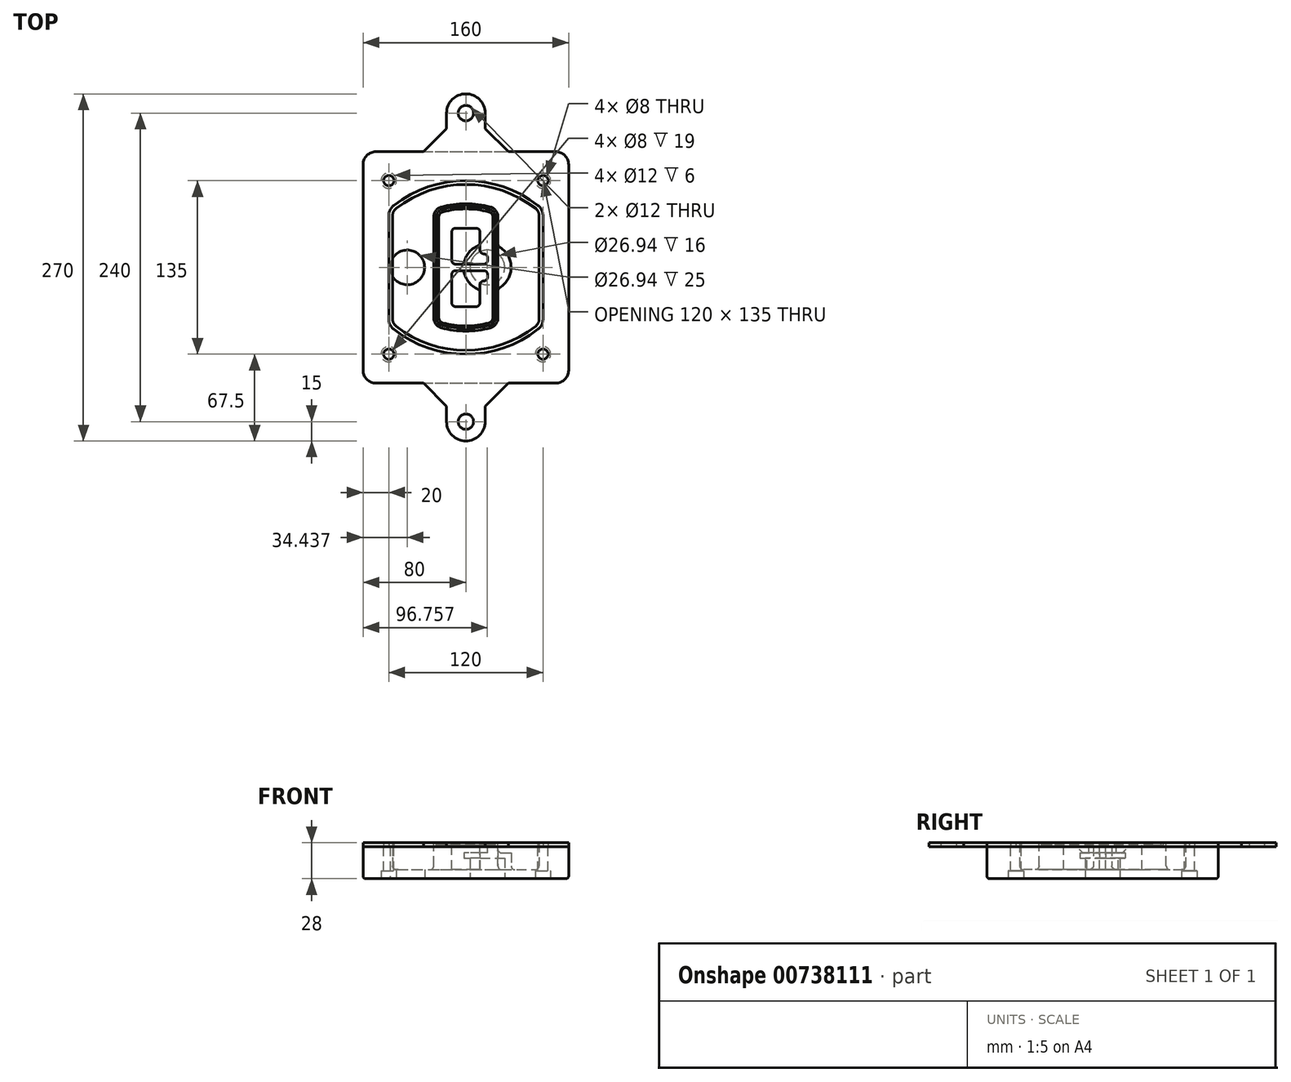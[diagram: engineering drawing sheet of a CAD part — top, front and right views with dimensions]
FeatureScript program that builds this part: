
annotation { "Feature Type Name" : "Feature", "Feature Type Description" : "" }
export const myFeature = defineFeature(function(context is Context, id is Id, definition is map)
    precondition{}
    {
        {
            var Q0;
            Q0=qCreatedBy(makeId("Top.planeOp"),FACE);
            var sketch = newSketch(context, id + "F0", { "sketchPlane" : qUnion([Q0])});
            skPoint(sketch, "E0.rect.middle", {"position": v(0, 0) * mm});
            skLineSegment(sketch, "E1.bottom", {"start": v(-70, -90) * mm, "end": v(70, -90) * mm});
            skLineSegment(sketch, "E1.top", {"start": v(-70, 90) * mm, "end": v(70, 90) * mm});
            skLineSegment(sketch, "E1.left", {"start": v(-80, -80) * mm, "end": v(-80, 80) * mm});
            skLineSegment(sketch, "E1.right", {"start": v(80, -80) * mm, "end": v(80, 80) * mm});
            skLineSegment(sketch, "E2", {"start": v(-80, 90) * mm, "end": v(80, -90) * mm, "construction": true});
            skLineSegment(sketch, "E3", {"start": v(80, 90) * mm, "end": v(-80, -90) * mm, "construction": true});
            skCircle(sketch, "E4", {"center": v(-60, 67.5) * mm, "radius": 4 * mm});
            skCircle(sketch, "E5", {"center": v(60, 67.5) * mm, "radius": 4 * mm});
            skCircle(sketch, "E6", {"center": v(60, -67.5) * mm, "radius": 4 * mm});
            skCircle(sketch, "E7", {"center": v(-60, -67.5) * mm, "radius": 4 * mm});
            skLineSegment(sketch, "E8", {"start": v(-60, 67.5) * mm, "end": v(60, 67.5) * mm, "construction": true});
            skLineSegment(sketch, "E9", {"start": v(60, 67.5) * mm, "end": v(60, -67.5) * mm, "construction": true});
            skLineSegment(sketch, "E10", {"start": v(60, -67.5) * mm, "end": v(-60, -67.5) * mm, "construction": true});
            skLineSegment(sketch, "E11", {"start": v(-60, -67.5) * mm, "end": v(-60, 67.5) * mm, "construction": true});
            skLineSegment(sketch, "E12", {"start": v(-60, 40.3) * mm, "end": v(-60, -40.3) * mm});
            skLineSegment(sketch, "E13", {"start": v(60, 40.3) * mm, "end": v(60, -40.3) * mm});
            skArc(sketch, "E14", {"start": v(56.15, 48.18) * mm, "mid": v(0, 67.5) * mm, "end": v(-56.15, 48.18) * mm});
            skArc(sketch, "E15", {"start": v(-56.15, -48.18) * mm, "mid": v(0, -67.5) * mm, "end": v(56.15, -48.18) * mm});
            skLineSegment(sketch, "E16", {"start": v(-60, 0) * mm, "end": v(60, 0) * mm, "construction": true});
            skPoint(sketch, "E17.visualSharp", {"position": v(-60, -45) * mm});
            skArc(sketch, "E17.filletArc", {"start": v(-60, -40.3) * mm, "mid": v(-58.99, -44.68) * mm, "end": v(-56.15, -48.18) * mm});
            skPoint(sketch, "E18.visualSharp", {"position": v(-60, 45) * mm});
            skArc(sketch, "E18.filletArc", {"start": v(-56.15, 48.18) * mm, "mid": v(-58.99, 44.68) * mm, "end": v(-60, 40.3) * mm});
            skPoint(sketch, "E19.visualSharp", {"position": v(60, 45) * mm});
            skArc(sketch, "E19.filletArc", {"start": v(60, 40.3) * mm, "mid": v(58.99, 44.68) * mm, "end": v(56.15, 48.18) * mm});
            skPoint(sketch, "E20.visualSharp", {"position": v(60, -45) * mm});
            skArc(sketch, "E20.filletArc", {"start": v(56.15, -48.18) * mm, "mid": v(58.99, -44.68) * mm, "end": v(60, -40.3) * mm});
            skPoint(sketch, "E21.visualSharp", {"position": v(-80, 90) * mm});
            skArc(sketch, "E21.filletArc", {"start": v(-70, 90) * mm, "mid": v(-77.07, 87.07) * mm, "end": v(-80, 80) * mm});
            skPoint(sketch, "E22.visualSharp", {"position": v(80, 90) * mm});
            skArc(sketch, "E22.filletArc", {"start": v(80, 80) * mm, "mid": v(77.07, 87.07) * mm, "end": v(70, 90) * mm});
            skPoint(sketch, "E23.visualSharp", {"position": v(80, -90) * mm});
            skArc(sketch, "E23.filletArc", {"start": v(70, -90) * mm, "mid": v(77.07, -87.07) * mm, "end": v(80, -80) * mm});
            skPoint(sketch, "E24.visualSharp", {"position": v(-80, -90) * mm});
            skArc(sketch, "E24.filletArc", {"start": v(-80, -80) * mm, "mid": v(-77.07, -87.07) * mm, "end": v(-70, -90) * mm});
            skArc(sketch, "E25.0", {"start": v(57, 40.3) * mm, "mid": v(56.3, 43.36) * mm, "end": v(54.3, 45.81) * mm});
            skLineSegment(sketch, "E25.1", {"start": v(57, 40.3) * mm, "end": v(57, -40.3) * mm});
            skArc(sketch, "E25.2", {"start": v(54.3, -45.81) * mm, "mid": v(56.3, -43.36) * mm, "end": v(57, -40.3) * mm});
            skArc(sketch, "E25.3", {"start": v(-54.3, -45.81) * mm, "mid": v(0, -64.5) * mm, "end": v(54.3, -45.81) * mm});
            skArc(sketch, "E25.4", {"start": v(-57, -40.3) * mm, "mid": v(-56.3, -43.36) * mm, "end": v(-54.3, -45.81) * mm});
            skArc(sketch, "E25.5", {"start": v(54.3, 45.81) * mm, "mid": v(0, 64.5) * mm, "end": v(-54.3, 45.81) * mm});
            skLineSegment(sketch, "E25.6", {"start": v(-57, 40.3) * mm, "end": v(-57, -40.3) * mm});
            skArc(sketch, "E25.7", {"start": v(-54.3, 45.81) * mm, "mid": v(-56.3, 43.36) * mm, "end": v(-57, 40.3) * mm});
            skArc(sketch, "E26.0", {"start": v(-58.62, 51.33) * mm, "mid": v(-62.58, 46.43) * mm, "end": v(-64, 40.3) * mm});
            skArc(sketch, "E26.1", {"start": v(58.62, 51.33) * mm, "mid": v(0, 71.5) * mm, "end": v(-58.62, 51.33) * mm});
            skArc(sketch, "E26.2", {"start": v(64, 40.3) * mm, "mid": v(62.58, 46.43) * mm, "end": v(58.62, 51.33) * mm});
            skLineSegment(sketch, "E26.3", {"start": v(64, 40.3) * mm, "end": v(64, -40.3) * mm});
            skArc(sketch, "E26.4", {"start": v(58.62, -51.33) * mm, "mid": v(62.58, -46.43) * mm, "end": v(64, -40.3) * mm});
            skLineSegment(sketch, "E26.5", {"start": v(-64, 40.3) * mm, "end": v(-64, -40.3) * mm});
            skArc(sketch, "E26.6", {"start": v(-58.62, -51.33) * mm, "mid": v(0, -71.5) * mm, "end": v(58.62, -51.33) * mm});
            skArc(sketch, "E26.7", {"start": v(-64, -40.3) * mm, "mid": v(-62.58, -46.43) * mm, "end": v(-58.62, -51.33) * mm});
            skSolve(sketch);
        }
        {
            var Q0;
            Q0=makeQuery(id+"F0.imprint","IMPRINT",FACE,{"disambiguationData":[TD([[makeQuery(id+"F0.imprint","IMPRINT",EDGE,{"derivedFrom":sQuery(id+"F0.wireOp",EDGE,"E1.bottom")}),1.0]])]});
            var Q1;
            Q1=makeQuery(id+"F0.imprint","IMPRINT",FACE,{"disambiguationData":[TD([[makeQuery(id+"F0.imprint","IMPRINT",EDGE,{"derivedFrom":sQuery(id+"F0.wireOp",EDGE,"E12")}),1.0]])]});
            var Q2;
            Q2=makeQuery(id+"F0.imprint","IMPRINT",FACE,{"disambiguationData":[TD([[makeQuery(id+"F0.imprint","IMPRINT",EDGE,{"derivedFrom":sQuery(id+"F0.wireOp",EDGE,"E25.0")}),1.0]])]});
            var Q3;
            Q3=makeQuery(id+"F0.imprint","IMPRINT",FACE,{"disambiguationData":[TD([[makeQuery(id+"F0.imprint","IMPRINT",EDGE,{"derivedFrom":sQuery(id+"F0.wireOp",EDGE,"E12")}),-1.0]])]});
            extrude(context, id + "F1", {"entities" : qUnion([Q0, Q1, Q2, Q3]), "oppositeDirection" : true, "depth" : 25 * mm});
        }
        {
            var Q0;
            Q0=makeQuery(id+"F0.imprint","IMPRINT",FACE,{"disambiguationData":[TD([[makeQuery(id+"F0.imprint","IMPRINT",EDGE,{"derivedFrom":sQuery(id+"F0.wireOp",EDGE,"E12")}),1.0]])]});
            extrude(context, id + "F2", {"entities" : qUnion([Q0]), "operationType" : NewBodyOperationType.ADD, "depth" : 3 * mm});
        }
        {
            var Q0;
            Q0=makeQuery(id+"F0.imprint","IMPRINT",FACE,{"disambiguationData":[TD([[makeQuery(id+"F0.imprint","IMPRINT",EDGE,{"derivedFrom":sQuery(id+"F0.wireOp",EDGE,"E25.0")}),1.0]])]});
            extrude(context, id + "F3", {"entities" : qUnion([Q0]), "operationType" : NewBodyOperationType.REMOVE, "oppositeDirection" : true, "depth" : 18 * mm});
        }
        {
            var Q0;
            Q0=makeQuery(id+"F2.opExtrude","CAP_FACE",FACE,{"disambiguationData":[OSD([sQuery(id+"F0.wireOp",EDGE,"E12"),sQuery(id+"F0.wireOp",EDGE,"E13"),sQuery(id+"F0.wireOp",EDGE,"E14"),sQuery(id+"F0.wireOp",EDGE,"E15"),sQuery(id+"F0.wireOp",EDGE,"E17.filletArc"),sQuery(id+"F0.wireOp",EDGE,"E18.filletArc"),sQuery(id+"F0.wireOp",EDGE,"E19.filletArc"),sQuery(id+"F0.wireOp",EDGE,"E20.filletArc"),sQuery(id+"F0.wireOp",EDGE,"E25.0"),sQuery(id+"F0.wireOp",EDGE,"E25.1"),sQuery(id+"F0.wireOp",EDGE,"E25.2"),sQuery(id+"F0.wireOp",EDGE,"E25.3"),sQuery(id+"F0.wireOp",EDGE,"E25.4"),sQuery(id+"F0.wireOp",EDGE,"E25.5"),sQuery(id+"F0.wireOp",EDGE,"E25.6"),sQuery(id+"F0.wireOp",EDGE,"E25.7")])],"isStart":false});
            var sketch = newSketch(context, id + "F4", { "sketchPlane" : qUnion([Q0])});
            skArc(sketch, "E27.0", {"start": v(-19.08, -46.97) * mm, "mid": v(0, -49.5) * mm, "end": v(19.08, -46.97) * mm});
            skArc(sketch, "E28.0", {"start": v(19.08, 46.97) * mm, "mid": v(0, 49.5) * mm, "end": v(-19.08, 46.97) * mm});
            skLineSegment(sketch, "E29", {"start": v(-25, 39.25) * mm, "end": v(-25, -39.25) * mm});
            skLineSegment(sketch, "E30", {"start": v(25, 39.25) * mm, "end": v(25, -39.25) * mm});
            skLineSegment(sketch, "E31", {"start": v(-25, 45.1) * mm, "end": v(25, 45.1) * mm, "construction": true});
            skLineSegment(sketch, "E32", {"start": v(-25, -45.1) * mm, "end": v(25, -45.1) * mm, "construction": true});
            skPoint(sketch, "E33.visualSharp", {"position": v(-25, 45.1) * mm});
            skArc(sketch, "E33.filletArc", {"start": v(-19.08, 46.97) * mm, "mid": v(-23.35, 44.11) * mm, "end": v(-25, 39.25) * mm});
            skPoint(sketch, "E34.visualSharp", {"position": v(25, 45.1) * mm});
            skArc(sketch, "E34.filletArc", {"start": v(25, 39.25) * mm, "mid": v(23.35, 44.11) * mm, "end": v(19.08, 46.97) * mm});
            skPoint(sketch, "E35.visualSharp", {"position": v(25, -45.1) * mm});
            skArc(sketch, "E35.filletArc", {"start": v(19.08, -46.97) * mm, "mid": v(23.35, -44.11) * mm, "end": v(25, -39.25) * mm});
            skPoint(sketch, "E36.visualSharp", {"position": v(-25, -45.1) * mm});
            skArc(sketch, "E36.filletArc", {"start": v(-25, -39.25) * mm, "mid": v(-23.35, -44.11) * mm, "end": v(-19.08, -46.97) * mm});
            skArc(sketch, "E37.0", {"start": v(54.3, 45.81) * mm, "mid": v(0, 64.5) * mm, "end": v(-54.3, 45.81) * mm});
            skArc(sketch, "E37.1", {"start": v(-54.3, 45.81) * mm, "mid": v(-56.3, 43.36) * mm, "end": v(-57, 40.3) * mm});
            skLineSegment(sketch, "E37.2", {"start": v(-57, 40.3) * mm, "end": v(-57, -40.3) * mm});
            skArc(sketch, "E37.3", {"start": v(-57, -40.3) * mm, "mid": v(-56.3, -43.36) * mm, "end": v(-54.3, -45.81) * mm});
            skArc(sketch, "E37.4", {"start": v(-54.3, -45.81) * mm, "mid": v(0, -64.5) * mm, "end": v(54.3, -45.81) * mm});
            skArc(sketch, "E37.5", {"start": v(54.3, -45.81) * mm, "mid": v(56.3, -43.36) * mm, "end": v(57, -40.3) * mm});
            skLineSegment(sketch, "E37.6", {"start": v(57, 40.3) * mm, "end": v(57, -40.3) * mm});
            skArc(sketch, "E37.7", {"start": v(57, 40.3) * mm, "mid": v(56.3, 43.36) * mm, "end": v(54.3, 45.81) * mm});
            skLineSegment(sketch, "E38.0", {"start": v(23, 39.25) * mm, "end": v(23, -39.25) * mm});
            skArc(sketch, "E38.1", {"start": v(18.56, -45.04) * mm, "mid": v(21.76, -42.9) * mm, "end": v(23, -39.25) * mm});
            skArc(sketch, "E38.2", {"start": v(-18.56, -45.04) * mm, "mid": v(0, -47.5) * mm, "end": v(18.56, -45.04) * mm});
            skArc(sketch, "E38.3", {"start": v(-23, -39.25) * mm, "mid": v(-21.76, -42.9) * mm, "end": v(-18.56, -45.04) * mm});
            skLineSegment(sketch, "E38.4", {"start": v(-23, 39.25) * mm, "end": v(-23, -39.25) * mm});
            skArc(sketch, "E38.5", {"start": v(23, 39.25) * mm, "mid": v(21.76, 42.9) * mm, "end": v(18.56, 45.04) * mm});
            skArc(sketch, "E38.6", {"start": v(-18.56, 45.04) * mm, "mid": v(-21.76, 42.9) * mm, "end": v(-23, 39.25) * mm});
            skArc(sketch, "E38.7", {"start": v(18.56, 45.04) * mm, "mid": v(0, 47.5) * mm, "end": v(-18.56, 45.04) * mm});
            skArc(sketch, "E39.0", {"start": v(21, 39.25) * mm, "mid": v(20.18, 41.68) * mm, "end": v(18.04, 43.1) * mm});
            skLineSegment(sketch, "E39.1", {"start": v(21, 39.25) * mm, "end": v(21, -39.25) * mm});
            skArc(sketch, "E39.2", {"start": v(18.04, -43.1) * mm, "mid": v(20.18, -41.68) * mm, "end": v(21, -39.25) * mm});
            skArc(sketch, "E39.3", {"start": v(-18.04, -43.1) * mm, "mid": v(0, -45.5) * mm, "end": v(18.04, -43.1) * mm});
            skArc(sketch, "E39.4", {"start": v(-21, -39.25) * mm, "mid": v(-20.18, -41.68) * mm, "end": v(-18.04, -43.1) * mm});
            skArc(sketch, "E39.5", {"start": v(18.04, 43.1) * mm, "mid": v(0, 45.5) * mm, "end": v(-18.04, 43.1) * mm});
            skLineSegment(sketch, "E39.6", {"start": v(-21, 39.25) * mm, "end": v(-21, -39.25) * mm});
            skArc(sketch, "E39.7", {"start": v(-18.04, 43.1) * mm, "mid": v(-20.18, 41.68) * mm, "end": v(-21, 39.25) * mm});
            skLineSegment(sketch, "E40", {"start": v(-25, 0) * mm, "end": v(25, 0) * mm, "construction": true});
            skLineSegment(sketch, "E41", {"start": v(-11, 5.5) * mm, "end": v(-11, 27.5) * mm});
            skLineSegment(sketch, "E42", {"start": v(-8, 30.5) * mm, "end": v(8, 30.5) * mm});
            skLineSegment(sketch, "E43", {"start": v(11, 27.5) * mm, "end": v(11, 13.5) * mm});
            skLineSegment(sketch, "E44", {"start": v(14, 10.5) * mm, "end": v(14, 10.5) * mm});
            skLineSegment(sketch, "E45", {"start": v(17, 7.5) * mm, "end": v(17, 5.5) * mm});
            skLineSegment(sketch, "E46", {"start": v(14, 2.5) * mm, "end": v(-8, 2.5) * mm});
            skPoint(sketch, "E47.visualSharp", {"position": v(-11, 30.5) * mm});
            skArc(sketch, "E47.filletArc", {"start": v(-8, 30.5) * mm, "mid": v(-10.12, 29.62) * mm, "end": v(-11, 27.5) * mm});
            skPoint(sketch, "E48.visualSharp", {"position": v(11, 30.5) * mm});
            skArc(sketch, "E48.filletArc", {"start": v(11, 27.5) * mm, "mid": v(10.12, 29.62) * mm, "end": v(8, 30.5) * mm});
            skPoint(sketch, "E49.visualSharp", {"position": v(11, 10.5) * mm});
            skArc(sketch, "E49.filletArc", {"start": v(11, 13.5) * mm, "mid": v(11.88, 11.38) * mm, "end": v(14, 10.5) * mm});
            skPoint(sketch, "E50.visualSharp", {"position": v(17, 10.5) * mm});
            skArc(sketch, "E50.filletArc", {"start": v(17, 7.5) * mm, "mid": v(16.12, 9.62) * mm, "end": v(14, 10.5) * mm});
            skPoint(sketch, "E51.visualSharp", {"position": v(17, 2.5) * mm});
            skArc(sketch, "E51.filletArc", {"start": v(14, 2.5) * mm, "mid": v(16.12, 3.38) * mm, "end": v(17, 5.5) * mm});
            skPoint(sketch, "E52.visualSharp", {"position": v(-11, 2.5) * mm});
            skArc(sketch, "E52.filletArc", {"start": v(-11, 5.5) * mm, "mid": v(-10.12, 3.38) * mm, "end": v(-8, 2.5) * mm});
            skLineSegment(sketch, "E53.0.MirrorCS", {"start": v(14, -2.5) * mm, "end": v(-8, -2.5) * mm});
            skArc(sketch, "E54.0.MirrorCS", {"start": v(-11, -5.5) * mm, "mid": v(-10.12, -3.38) * mm, "end": v(-8, -2.5) * mm});
            skLineSegment(sketch, "E55.0.MirrorCS", {"start": v(-11, -5.5) * mm, "end": v(-11, -27.5) * mm});
            skArc(sketch, "E56.0.MirrorCS", {"start": v(-8, -30.5) * mm, "mid": v(-10.12, -29.62) * mm, "end": v(-11, -27.5) * mm});
            skLineSegment(sketch, "E57.0.MirrorCS", {"start": v(-8, -30.5) * mm, "end": v(8, -30.5) * mm});
            skArc(sketch, "E58.0.MirrorCS", {"start": v(11, -27.5) * mm, "mid": v(10.12, -29.62) * mm, "end": v(8, -30.5) * mm});
            skLineSegment(sketch, "E59.0.MirrorCS", {"start": v(11, -27.5) * mm, "end": v(11, -13.5) * mm});
            skArc(sketch, "E60.0.MirrorCS", {"start": v(11, -13.5) * mm, "mid": v(11.88, -11.38) * mm, "end": v(14, -10.5) * mm});
            skArc(sketch, "E61.0.MirrorCS", {"start": v(17, -7.5) * mm, "mid": v(16.12, -9.62) * mm, "end": v(14, -10.5) * mm});
            skLineSegment(sketch, "E62.0.MirrorCS", {"start": v(17, -7.5) * mm, "end": v(17, -5.5) * mm});
            skArc(sketch, "E63.0.MirrorCS", {"start": v(14, -2.5) * mm, "mid": v(16.12, -3.38) * mm, "end": v(17, -5.5) * mm});
            skSolve(sketch);
        }
        {
            var Q0;
            Q0=makeQuery(id+"F4.imprint","IMPRINT",FACE,{"disambiguationData":[TD([[makeQuery(id+"F4.imprint","IMPRINT",EDGE,{"derivedFrom":sQuery(id+"F4.wireOp",EDGE,"E27.0")}),1.0]])]});
            var Q1;
            Q1=makeQuery(id+"F4.imprint","IMPRINT",FACE,{"disambiguationData":[TD([[makeQuery(id+"F4.imprint","IMPRINT",EDGE,{"derivedFrom":sQuery(id+"F4.wireOp",EDGE,"E38.0")}),-1.0]])]});
            var Q2;
            Q2=makeQuery(id+"F4.imprint","IMPRINT",FACE,{"disambiguationData":[TD([[makeQuery(id+"F4.imprint","IMPRINT",EDGE,{"derivedFrom":sQuery(id+"F4.wireOp",EDGE,"E39.0")}),1.0]])]});
            extrude(context, id + "F5", {"entities" : qUnion([Q0, Q1, Q2]), "operationType" : NewBodyOperationType.ADD, "endBound" : BoundingType.UP_TO_NEXT, "oppositeDirection" : true, "depth" : 25 * mm});
        }
        {
            var Q0;
            Q0=makeQuery(id+"F4.imprint","IMPRINT",FACE,{"disambiguationData":[TD([[makeQuery(id+"F4.imprint","IMPRINT",EDGE,{"derivedFrom":sQuery(id+"F4.wireOp",EDGE,"E38.0")}),-1.0]])]});
            extrude(context, id + "F6", {"entities" : qUnion([Q0]), "operationType" : NewBodyOperationType.REMOVE, "oppositeDirection" : true, "depth" : 2 * mm});
        }
        {
            var Q0;
            Q0=makeQuery(id+"F1.opExtrude","CAP_FACE",FACE,{"disambiguationData":[OSD([sQuery(id+"F0.wireOp",EDGE,"E1.bottom"),sQuery(id+"F0.wireOp",EDGE,"E1.top"),sQuery(id+"F0.wireOp",EDGE,"E1.left"),sQuery(id+"F0.wireOp",EDGE,"E1.right"),sQuery(id+"F0.wireOp",EDGE,"E4"),sQuery(id+"F0.wireOp",EDGE,"E5"),sQuery(id+"F0.wireOp",EDGE,"E6"),sQuery(id+"F0.wireOp",EDGE,"E7"),sQuery(id+"F0.wireOp",EDGE,"E21.filletArc"),sQuery(id+"F0.wireOp",EDGE,"E22.filletArc"),sQuery(id+"F0.wireOp",EDGE,"E23.filletArc"),sQuery(id+"F0.wireOp",EDGE,"E24.filletArc")])],"isStart":false});
            var sketch = newSketch(context, id + "F7", { "sketchPlane" : qUnion([Q0])});
            skCircle(sketch, "E64", {"center": v(16.76, 0) * mm, "radius": 13.47 * mm});
            skCircle(sketch, "E65", {"center": v(-45.56, 0) * mm, "radius": 13.47 * mm});
            skLineSegment(sketch, "E66", {"start": v(80, 0) * mm, "end": v(-80, 0) * mm});
            skCircle(sketch, "E67", {"center": v(16.76, 0) * mm, "radius": 18.47 * mm});
            skCircle(sketch, "E68", {"center": v(60, -67.5) * mm, "radius": 6 * mm});
            skCircle(sketch, "E69", {"center": v(-60, -67.5) * mm, "radius": 6 * mm});
            skCircle(sketch, "E70", {"center": v(-60, 67.5) * mm, "radius": 6 * mm});
            skCircle(sketch, "E71", {"center": v(60, 67.5) * mm, "radius": 6 * mm});
            skSolve(sketch);
        }
        {
            var Q0;
            {var subQ1=sQuery(id+"F7.wireOp",EDGE,"E66");var subQ4=sQuery(id+"F7.wireOp",EDGE,"E64");var subQ6=makeQuery(id+"F7.imprint","INTERSECT",VERTEX,{"disambiguationData":[OD(0.0)],"derivedFrom":[subQ4,subQ1]});Q0=makeQuery(id+"F7.imprint","IMPRINT",FACE,{"disambiguationData":[TD([[makeQuery(id+"F7.imprint","IMPRINT",EDGE,{"disambiguationData":[TD([[subQ6,-1.0]])],"derivedFrom":subQ4}),-1.0]])]});}
            var Q1;
            {var subQ0=sQuery(id+"F7.wireOp",EDGE,"E66");var subQ1=sQuery(id+"F7.wireOp",EDGE,"E64");var subQ3=makeQuery(id+"F7.imprint","INTERSECT",VERTEX,{"disambiguationData":[OD(0.0)],"derivedFrom":[subQ1,subQ0]});Q1=makeQuery(id+"F7.imprint","IMPRINT",FACE,{"disambiguationData":[TD([[makeQuery(id+"F7.imprint","IMPRINT",EDGE,{"disambiguationData":[TD([[subQ3,-1.0]])],"derivedFrom":subQ1}),1.0]])]});}
            var Q2;
            {var subQ0=sQuery(id+"F7.wireOp",EDGE,"E66");var subQ1=sQuery(id+"F7.wireOp",EDGE,"E64");var subQ3=makeQuery(id+"F7.imprint","INTERSECT",VERTEX,{"disambiguationData":[OD(0.0)],"derivedFrom":[subQ1,subQ0]});Q2=makeQuery(id+"F7.imprint","IMPRINT",FACE,{"disambiguationData":[TD([[makeQuery(id+"F7.imprint","IMPRINT",EDGE,{"disambiguationData":[TD([[subQ3,1.0]])],"derivedFrom":subQ1}),1.0]])]});}
            var Q3;
            {var subQ1=sQuery(id+"F7.wireOp",EDGE,"E66");var subQ4=sQuery(id+"F7.wireOp",EDGE,"E64");var subQ6=makeQuery(id+"F7.imprint","INTERSECT",VERTEX,{"disambiguationData":[OD(0.0)],"derivedFrom":[subQ4,subQ1]});Q3=makeQuery(id+"F7.imprint","IMPRINT",FACE,{"disambiguationData":[TD([[makeQuery(id+"F7.imprint","IMPRINT",EDGE,{"disambiguationData":[TD([[subQ6,1.0]])],"derivedFrom":subQ4}),-1.0]])]});}
            extrude(context, id + "F8", {"entities" : qUnion([Q0, Q1, Q2, Q3]), "operationType" : NewBodyOperationType.ADD, "oppositeDirection" : true, "depth" : 20 * mm});
        }
        {
            var Q0;
            {var subQ0=sQuery(id+"F7.wireOp",EDGE,"E66");var subQ1=sQuery(id+"F7.wireOp",EDGE,"E64");var subQ3=makeQuery(id+"F7.imprint","INTERSECT",VERTEX,{"disambiguationData":[OD(0.0)],"derivedFrom":[subQ1,subQ0]});Q0=makeQuery(id+"F7.imprint","IMPRINT",FACE,{"disambiguationData":[TD([[makeQuery(id+"F7.imprint","IMPRINT",EDGE,{"disambiguationData":[TD([[subQ3,-1.0]])],"derivedFrom":subQ1}),1.0]])]});}
            var Q1;
            {var subQ0=sQuery(id+"F7.wireOp",EDGE,"E66");var subQ1=sQuery(id+"F7.wireOp",EDGE,"E64");var subQ3=makeQuery(id+"F7.imprint","INTERSECT",VERTEX,{"disambiguationData":[OD(0.0)],"derivedFrom":[subQ1,subQ0]});Q1=makeQuery(id+"F7.imprint","IMPRINT",FACE,{"disambiguationData":[TD([[makeQuery(id+"F7.imprint","IMPRINT",EDGE,{"disambiguationData":[TD([[subQ3,1.0]])],"derivedFrom":subQ1}),1.0]])]});}
            extrude(context, id + "F9", {"entities" : qUnion([Q0, Q1]), "operationType" : NewBodyOperationType.REMOVE, "oppositeDirection" : true, "depth" : 16 * mm});
        }
        {
            var Q0;
            {var subQ0=sQuery(id+"F7.wireOp",EDGE,"E66");var subQ1=sQuery(id+"F7.wireOp",EDGE,"E65");var subQ3=makeQuery(id+"F7.imprint","INTERSECT",VERTEX,{"disambiguationData":[OD(0.0)],"derivedFrom":[subQ1,subQ0]});Q0=makeQuery(id+"F7.imprint","IMPRINT",FACE,{"disambiguationData":[TD([[makeQuery(id+"F7.imprint","IMPRINT",EDGE,{"disambiguationData":[TD([[subQ3,-1.0]])],"derivedFrom":subQ1}),1.0]])]});}
            var Q1;
            {var subQ0=sQuery(id+"F7.wireOp",EDGE,"E66");var subQ1=sQuery(id+"F7.wireOp",EDGE,"E65");var subQ3=makeQuery(id+"F7.imprint","INTERSECT",VERTEX,{"disambiguationData":[OD(0.0)],"derivedFrom":[subQ1,subQ0]});Q1=makeQuery(id+"F7.imprint","IMPRINT",FACE,{"disambiguationData":[TD([[makeQuery(id+"F7.imprint","IMPRINT",EDGE,{"disambiguationData":[TD([[subQ3,1.0]])],"derivedFrom":subQ1}),1.0]])]});}
            extrude(context, id + "F10", {"entities" : qUnion([Q0, Q1]), "operationType" : NewBodyOperationType.REMOVE, "oppositeDirection" : true, "depth" : 25 * mm});
        }
        {
            var Q0;
            Q0=makeQuery(id+"F7.imprint","IMPRINT",FACE,{"disambiguationData":[TD([[makeQuery(id+"F7.imprint","IMPRINT",EDGE,{"derivedFrom":sQuery(id+"F7.wireOp",EDGE,"E68")}),1.0]])]});
            var Q1;
            Q1=makeQuery(id+"F7.imprint","IMPRINT",FACE,{"disambiguationData":[TD([[makeQuery(id+"F7.imprint","IMPRINT",EDGE,{"derivedFrom":makeQuery(id+"F1.opExtrude","CAP_EDGE",EDGE,{"disambiguationData":[OSD([sQuery(id+"F0.wireOp",EDGE,"E5")])],"isStart":false})}),-1.0]])]});
            var Q2;
            Q2=makeQuery(id+"F7.imprint","IMPRINT",FACE,{"disambiguationData":[TD([[makeQuery(id+"F7.imprint","IMPRINT",EDGE,{"derivedFrom":sQuery(id+"F7.wireOp",EDGE,"E69")}),1.0]])]});
            var Q3;
            Q3=makeQuery(id+"F7.imprint","IMPRINT",FACE,{"disambiguationData":[TD([[makeQuery(id+"F7.imprint","IMPRINT",EDGE,{"derivedFrom":makeQuery(id+"F1.opExtrude","CAP_EDGE",EDGE,{"disambiguationData":[OSD([sQuery(id+"F0.wireOp",EDGE,"E4")])],"isStart":false})}),-1.0]])]});
            var Q4;
            Q4=makeQuery(id+"F7.imprint","IMPRINT",FACE,{"disambiguationData":[TD([[makeQuery(id+"F7.imprint","IMPRINT",EDGE,{"derivedFrom":sQuery(id+"F7.wireOp",EDGE,"E70")}),1.0]])]});
            var Q5;
            Q5=makeQuery(id+"F7.imprint","IMPRINT",FACE,{"disambiguationData":[TD([[makeQuery(id+"F7.imprint","IMPRINT",EDGE,{"derivedFrom":makeQuery(id+"F1.opExtrude","CAP_EDGE",EDGE,{"disambiguationData":[OSD([sQuery(id+"F0.wireOp",EDGE,"E7")])],"isStart":false})}),-1.0]])]});
            var Q6;
            Q6=makeQuery(id+"F7.imprint","IMPRINT",FACE,{"disambiguationData":[TD([[makeQuery(id+"F7.imprint","IMPRINT",EDGE,{"derivedFrom":sQuery(id+"F7.wireOp",EDGE,"E71")}),1.0]])]});
            var Q7;
            Q7=makeQuery(id+"F7.imprint","IMPRINT",FACE,{"disambiguationData":[TD([[makeQuery(id+"F7.imprint","IMPRINT",EDGE,{"derivedFrom":makeQuery(id+"F1.opExtrude","CAP_EDGE",EDGE,{"disambiguationData":[OSD([sQuery(id+"F0.wireOp",EDGE,"E6")])],"isStart":false})}),-1.0]])]});
            extrude(context, id + "F11", {"entities" : qUnion([Q0, Q1, Q2, Q3, Q4, Q5, Q6, Q7]), "operationType" : NewBodyOperationType.REMOVE, "oppositeDirection" : true, "depth" : 6 * mm});
        }
        {
            var Q0;
            Q0=makeQuery(id+"F9.boolean.opBoolean","COPY",FACE,{"derivedFrom":makeQuery(id+"F9.opExtrude","CAP_FACE",FACE,{"disambiguationData":[OSD([sQuery(id+"F7.wireOp",EDGE,"E64")])],"isStart":false})});
            var sketch = newSketch(context, id + "F12", { "sketchPlane" : qUnion([Q0])});
            skArc(sketch, "E72.0", {"start": v(11, 17.55) * mm, "mid": v(2.57, 11.82) * mm, "end": v(-1.54, 2.5) * mm});
            skArc(sketch, "E72.1", {"start": v(-1.54, -2.5) * mm, "mid": v(2.57, -11.82) * mm, "end": v(11, -17.55) * mm});
            skLineSegment(sketch, "E73", {"start": v(-1.54, -2.5) * mm, "end": v(14, -2.5) * mm});
            skLineSegment(sketch, "E74.0", {"start": v(14, 2.5) * mm, "end": v(-1.54, 2.5) * mm});
            skArc(sketch, "E74.1", {"start": v(14, 2.5) * mm, "mid": v(16.12, 3.38) * mm, "end": v(17, 5.5) * mm});
            skLineSegment(sketch, "E74.2", {"start": v(17, 7.5) * mm, "end": v(17, 5.5) * mm});
            skArc(sketch, "E74.3", {"start": v(17, 7.5) * mm, "mid": v(16.12, 9.62) * mm, "end": v(14, 10.5) * mm});
            skArc(sketch, "E74.4", {"start": v(11, 13.5) * mm, "mid": v(11.88, 11.38) * mm, "end": v(14, 10.5) * mm});
            skLineSegment(sketch, "E74.5", {"start": v(11, 17.55) * mm, "end": v(11, 13.5) * mm});
            skLineSegment(sketch, "E74.7", {"start": v(14, -2.5) * mm, "end": v(-1.54, -2.5) * mm});
            skArc(sketch, "E74.8", {"start": v(14, -2.5) * mm, "mid": v(16.12, -3.38) * mm, "end": v(17, -5.5) * mm});
            skLineSegment(sketch, "E74.9", {"start": v(17, -7.5) * mm, "end": v(17, -5.5) * mm});
            skArc(sketch, "E74.10", {"start": v(17, -7.5) * mm, "mid": v(16.12, -9.62) * mm, "end": v(14, -10.5) * mm});
            skArc(sketch, "E74.11", {"start": v(11, -13.5) * mm, "mid": v(11.88, -11.38) * mm, "end": v(14, -10.5) * mm});
            skLineSegment(sketch, "E74.12", {"start": v(11, -17.55) * mm, "end": v(11, -13.5) * mm});
            skPoint(sketch, "E75.orphan", {"position": v(11, -27.5) * mm});
            skPoint(sketch, "E76.orphan", {"position": v(-8, -2.5) * mm});
            skPoint(sketch, "E77.orphan", {"position": v(-8, 2.5) * mm});
            skPoint(sketch, "E78.orphan", {"position": v(11, 27.5) * mm});
            skSolve(sketch);
        }
        {
            var Q0;
            {var subQ7=sQuery(id+"F12.wireOp",EDGE,"E72.0");var subQ14=sQuery(id+"F12.wireOp",EDGE,"E72.1");var subQ16=sQuery(id+"F12.wireOp",EDGE,"E74.1");var subQ18=sQuery(id+"F12.wireOp",EDGE,"E74.8");Q0=qUnion([makeQuery(id+"F12.imprint","IMPRINT",FACE,{"disambiguationData":[TD([[makeQuery(id+"F12.imprint","IMPRINT",EDGE,{"derivedFrom":subQ7}),1.0]])]}),makeQuery(id+"F12.imprint","IMPRINT",FACE,{"disambiguationData":[TD([[makeQuery(id+"F12.imprint","IMPRINT",EDGE,{"derivedFrom":subQ14}),1.0]])]}),makeQuery(id+"F12.imprint","IMPRINT",FACE,{"disambiguationData":[TD([[makeQuery(id+"F12.imprint","IMPRINT",EDGE,{"derivedFrom":subQ16}),1.0]])]}),makeQuery(id+"F12.imprint","IMPRINT",FACE,{"disambiguationData":[TD([[makeQuery(id+"F12.imprint","IMPRINT",EDGE,{"derivedFrom":subQ18}),-1.0]])]})]);}
            var Q1;
            Q1=makeQuery(id+"F5.boolean.opBoolean","SPLIT",FACE,{"disambiguationData":[TD([makeQuery(id+"F5.opExtrude","SWEPT_FACE",FACE,{"disambiguationData":[OSD([sQuery(id+"F4.wireOp",EDGE,"E41")])]})])],"derivedFrom":makeQuery(id+"F3.boolean.opBoolean","COPY",FACE,{"derivedFrom":makeQuery(id+"F3.opExtrude","CAP_FACE",FACE,{"disambiguationData":[OSD([sQuery(id+"F0.wireOp",EDGE,"E25.0"),sQuery(id+"F0.wireOp",EDGE,"E25.1"),sQuery(id+"F0.wireOp",EDGE,"E25.2"),sQuery(id+"F0.wireOp",EDGE,"E25.3"),sQuery(id+"F0.wireOp",EDGE,"E25.4"),sQuery(id+"F0.wireOp",EDGE,"E25.5"),sQuery(id+"F0.wireOp",EDGE,"E25.6"),sQuery(id+"F0.wireOp",EDGE,"E25.7")])],"isStart":false})})});
            extrude(context, id + "F13", {"entities" : qUnion([Q0]), "operationType" : NewBodyOperationType.REMOVE, "endBound" : BoundingType.UP_TO_SURFACE, "endBoundEntityFace" : qUnion([Q1]), "depth" : 25 * mm});
        }
        {
            var Q0;
            Q0=makeQuery(id+"F3.boolean.opBoolean","COPY",EDGE,{"derivedFrom":makeQuery(id+"F3.opExtrude","CAP_EDGE",EDGE,{"disambiguationData":[OSD([sQuery(id+"F0.wireOp",EDGE,"E25.6")])],"isStart":false})});
            var Q1;
            Q1=makeQuery(id+"F8.boolean.opBoolean","INTERSECT",EDGE,{"derivedFrom":[makeQuery(id+"F5.opExtrude","SWEPT_FACE",FACE,{"disambiguationData":[OSD([sQuery(id+"F4.wireOp",EDGE,"E30")])]}),makeQuery(id+"F8.opExtrude","CAP_FACE",FACE,{"disambiguationData":[OSD([sQuery(id+"F7.wireOp",EDGE,"E67")])],"isStart":false})]});
            var Q2;
            Q2=makeQuery(id+"F8.boolean.opBoolean","INTERSECT",EDGE,{"disambiguationData":[OD(1.0)],"derivedFrom":[makeQuery(id+"F5.opExtrude","SWEPT_FACE",FACE,{"disambiguationData":[OSD([sQuery(id+"F4.wireOp",EDGE,"E30")])]}),makeQuery(id+"F8.opExtrude","SWEPT_FACE",FACE,{"disambiguationData":[OSD([sQuery(id+"F7.wireOp",EDGE,"E67")])]})]});
            var Q3;
            {var subQ0=sQuery(id+"F4.wireOp",EDGE,"E30");Q3=makeQuery(id+"F8.boolean.opBoolean","SPLIT",EDGE,{"disambiguationData":[TD([makeQuery(id+"F5.opExtrude","SWEPT_FACE",FACE,{"disambiguationData":[OSD([sQuery(id+"F4.wireOp",EDGE,"E35.filletArc")])]})])],"derivedFrom":makeQuery(id+"F5.opExtrude","CAP_EDGE",EDGE,{"disambiguationData":[OSD([subQ0])],"isStart":false})});}
            var Q4;
            {var subQ0=sQuery(id+"F0.wireOp",EDGE,"E25.7");var subQ1=sQuery(id+"F0.wireOp",EDGE,"E25.1");var subQ2=sQuery(id+"F0.wireOp",EDGE,"E25.6");var subQ3=sQuery(id+"F0.wireOp",EDGE,"E25.5");var subQ4=sQuery(id+"F0.wireOp",EDGE,"E25.4");var subQ5=sQuery(id+"F0.wireOp",EDGE,"E25.0");var subQ6=sQuery(id+"F0.wireOp",EDGE,"E25.2");var subQ7=sQuery(id+"F0.wireOp",EDGE,"E25.3");Q4=makeQuery(id+"F8.boolean.opBoolean","INTERSECT",EDGE,{"derivedFrom":[makeQuery(id+"F5.boolean.opBoolean","SPLIT",FACE,{"disambiguationData":[TD([makeQuery(id+"F2.opExtrude","SWEPT_FACE",FACE,{"disambiguationData":[OSD([subQ5])]})])],"derivedFrom":makeQuery(id+"F3.boolean.opBoolean","COPY",FACE,{"derivedFrom":makeQuery(id+"F3.opExtrude","CAP_FACE",FACE,{"disambiguationData":[OSD([subQ5,subQ1,subQ6,subQ7,subQ4,subQ3,subQ2,subQ0])],"isStart":false})})}),makeQuery(id+"F8.opExtrude","SWEPT_FACE",FACE,{"disambiguationData":[OSD([sQuery(id+"F7.wireOp",EDGE,"E67")])]})]});}
            var Q5;
            Q5=makeQuery(id+"F8.boolean.opBoolean","INTERSECT",EDGE,{"disambiguationData":[OD(0.0)],"derivedFrom":[makeQuery(id+"F5.opExtrude","SWEPT_FACE",FACE,{"disambiguationData":[OSD([sQuery(id+"F4.wireOp",EDGE,"E30")])]}),makeQuery(id+"F8.opExtrude","SWEPT_FACE",FACE,{"disambiguationData":[OSD([sQuery(id+"F7.wireOp",EDGE,"E67")])]})]});
            fillet(context, id + "F14", {"entities" : qUnion([Q0, Q1, Q2, Q3, Q4, Q5]), "radius" : 3 * mm, "tangentPropagation" : true, "allowEdgeOverflow" : false});
        }
        {
            var Q0;
            Q0=makeQuery(id+"F1.opExtrude","CAP_EDGE",EDGE,{"disambiguationData":[OSD([sQuery(id+"F0.wireOp",EDGE,"E1.bottom")])],"isStart":false});
            fillet(context, id + "F15", {"entities" : qUnion([Q0]), "radius" : 2 * mm, "tangentPropagation" : true, "allowEdgeOverflow" : false});
        }
        {
            var Q0;
            {var subQ0=sQuery(id+"F0.wireOp",EDGE,"E21.filletArc");var subQ1=sQuery(id+"F0.wireOp",EDGE,"E7");var subQ2=sQuery(id+"F0.wireOp",EDGE,"E6");var subQ3=sQuery(id+"F0.wireOp",EDGE,"E5");var subQ4=sQuery(id+"F0.wireOp",EDGE,"E4");var subQ5=sQuery(id+"F0.wireOp",EDGE,"E22.filletArc");var subQ6=sQuery(id+"F0.wireOp",EDGE,"E1.bottom");var subQ7=sQuery(id+"F0.wireOp",EDGE,"E1.right");var subQ8=sQuery(id+"F0.wireOp",EDGE,"E1.top");var subQ9=sQuery(id+"F0.wireOp",EDGE,"E1.left");var subQ10=sQuery(id+"F0.wireOp",EDGE,"E23.filletArc");var subQ11=sQuery(id+"F0.wireOp",EDGE,"E24.filletArc");Q0=makeQuery(id+"F2.boolean.opBoolean","SPLIT",FACE,{"disambiguationData":[TD([makeQuery(id+"F1.opExtrude","SWEPT_FACE",FACE,{"disambiguationData":[OSD([subQ6])]})])],"derivedFrom":makeQuery(id+"F1.opExtrude","CAP_FACE",FACE,{"disambiguationData":[OSD([subQ6,subQ8,subQ9,subQ7,subQ4,subQ3,subQ2,subQ1,subQ0,subQ5,subQ10,subQ11])],"isStart":true})});}
            var sketch = newSketch(context, id + "F16", { "sketchPlane" : qUnion([Q0])});
            skLineSegment(sketch, "E79.0", {"start": v(-80, -80) * mm, "end": v(-80, 80) * mm});
            skArc(sketch, "E79.1", {"start": v(-70, 90) * mm, "mid": v(-77.07, 87.07) * mm, "end": v(-80, 80) * mm});
            skLineSegment(sketch, "E79.2", {"start": v(-70, 90) * mm, "end": v(70, 90) * mm});
            skArc(sketch, "E79.3", {"start": v(80, 80) * mm, "mid": v(77.07, 87.07) * mm, "end": v(70, 90) * mm});
            skLineSegment(sketch, "E79.4", {"start": v(80, -80) * mm, "end": v(80, 80) * mm});
            skArc(sketch, "E79.5", {"start": v(70, -90) * mm, "mid": v(77.07, -87.07) * mm, "end": v(80, -80) * mm});
            skLineSegment(sketch, "E79.6", {"start": v(-70, -90) * mm, "end": v(70, -90) * mm});
            skArc(sketch, "E79.7", {"start": v(-80, -80) * mm, "mid": v(-77.07, -87.07) * mm, "end": v(-70, -90) * mm});
            skLineSegment(sketch, "E80", {"start": v(0, 90) * mm, "end": v(0, 120) * mm, "construction": true});
            skCircle(sketch, "E81", {"center": v(0, 120) * mm, "radius": 6 * mm});
            skLineSegment(sketch, "E82", {"start": v(-33, 90) * mm, "end": v(-15, 108) * mm});
            skLineSegment(sketch, "E83", {"start": v(-15, 108) * mm, "end": v(-15, 120) * mm});
            skLineSegment(sketch, "E84", {"start": v(15, 108) * mm, "end": v(15, 120) * mm});
            skArc(sketch, "E85", {"start": v(15, 120) * mm, "mid": v(0, 135) * mm, "end": v(-15, 120) * mm});
            skLineSegment(sketch, "E86", {"start": v(-80, 0) * mm, "end": v(80, 0) * mm, "construction": true});
            skLineSegment(sketch, "E87.MirrorCS", {"start": v(-33, -90) * mm, "end": v(-15, -108) * mm});
            skCircle(sketch, "E88.MirrorC", {"center": v(0, -120) * mm, "radius": 6 * mm});
            skLineSegment(sketch, "E89.MirrorCS", {"start": v(0, -90) * mm, "end": v(0, -120) * mm, "construction": true});
            skLineSegment(sketch, "E90.MirrorCS", {"start": v(-15, -108) * mm, "end": v(-15, -120) * mm});
            skLineSegment(sketch, "E91.MirrorCS", {"start": v(15, -108) * mm, "end": v(15, -120) * mm});
            skArc(sketch, "E92.MirrorCS", {"start": v(15, -120) * mm, "mid": v(0, -135) * mm, "end": v(-15, -120) * mm});
            skLineSegment(sketch, "E93", {"start": v(15, 108) * mm, "end": v(33, 90) * mm});
            skLineSegment(sketch, "E94.MirrorCS", {"start": v(15, -108) * mm, "end": v(33, -90) * mm});
            skSolve(sketch);
        }
        {
            var Q0;
            Q0=makeQuery(id+"F16.imprint","IMPRINT",FACE,{"disambiguationData":[TD([[makeQuery(id+"F16.imprint","IMPRINT",EDGE,{"derivedFrom":sQuery(id+"F16.wireOp",EDGE,"E81")}),-1.0]])]});
            var Q1;
            {var subQ0=sQuery(id+"F16.wireOp",EDGE,"E87.MirrorCS");Q1=makeQuery(id+"F16.imprint","IMPRINT",FACE,{"disambiguationData":[TD([[makeQuery(id+"F16.imprint","IMPRINT",EDGE,{"derivedFrom":subQ0}),1.0]])]});}
            var Q2;
            Q2=makeQuery(id+"F16.imprint","IMPRINT",FACE,{"disambiguationData":[TD([[makeQuery(id+"F16.imprint","IMPRINT",EDGE,{"derivedFrom":sQuery(id+"F16.wireOp",EDGE,"E79.0")}),-1.0]])]});
            var Q3;
            Q3=makeQuery(id+"F2.opExtrude","CAP_FACE",FACE,{"disambiguationData":[OSD([sQuery(id+"F0.wireOp",EDGE,"E12"),sQuery(id+"F0.wireOp",EDGE,"E13"),sQuery(id+"F0.wireOp",EDGE,"E14"),sQuery(id+"F0.wireOp",EDGE,"E15"),sQuery(id+"F0.wireOp",EDGE,"E17.filletArc"),sQuery(id+"F0.wireOp",EDGE,"E18.filletArc"),sQuery(id+"F0.wireOp",EDGE,"E19.filletArc"),sQuery(id+"F0.wireOp",EDGE,"E20.filletArc"),sQuery(id+"F0.wireOp",EDGE,"E25.0"),sQuery(id+"F0.wireOp",EDGE,"E25.1"),sQuery(id+"F0.wireOp",EDGE,"E25.2"),sQuery(id+"F0.wireOp",EDGE,"E25.3"),sQuery(id+"F0.wireOp",EDGE,"E25.4"),sQuery(id+"F0.wireOp",EDGE,"E25.5"),sQuery(id+"F0.wireOp",EDGE,"E25.6"),sQuery(id+"F0.wireOp",EDGE,"E25.7")])],"isStart":false});
            extrude(context, id + "F17", {"entities" : qUnion([Q0, Q1, Q2]), "endBound" : BoundingType.UP_TO_SURFACE, "depth" : 25 * mm, "endBoundEntityFace" : qUnion([Q3]), "offsetDistance" : 25 * mm});
        }
    });
